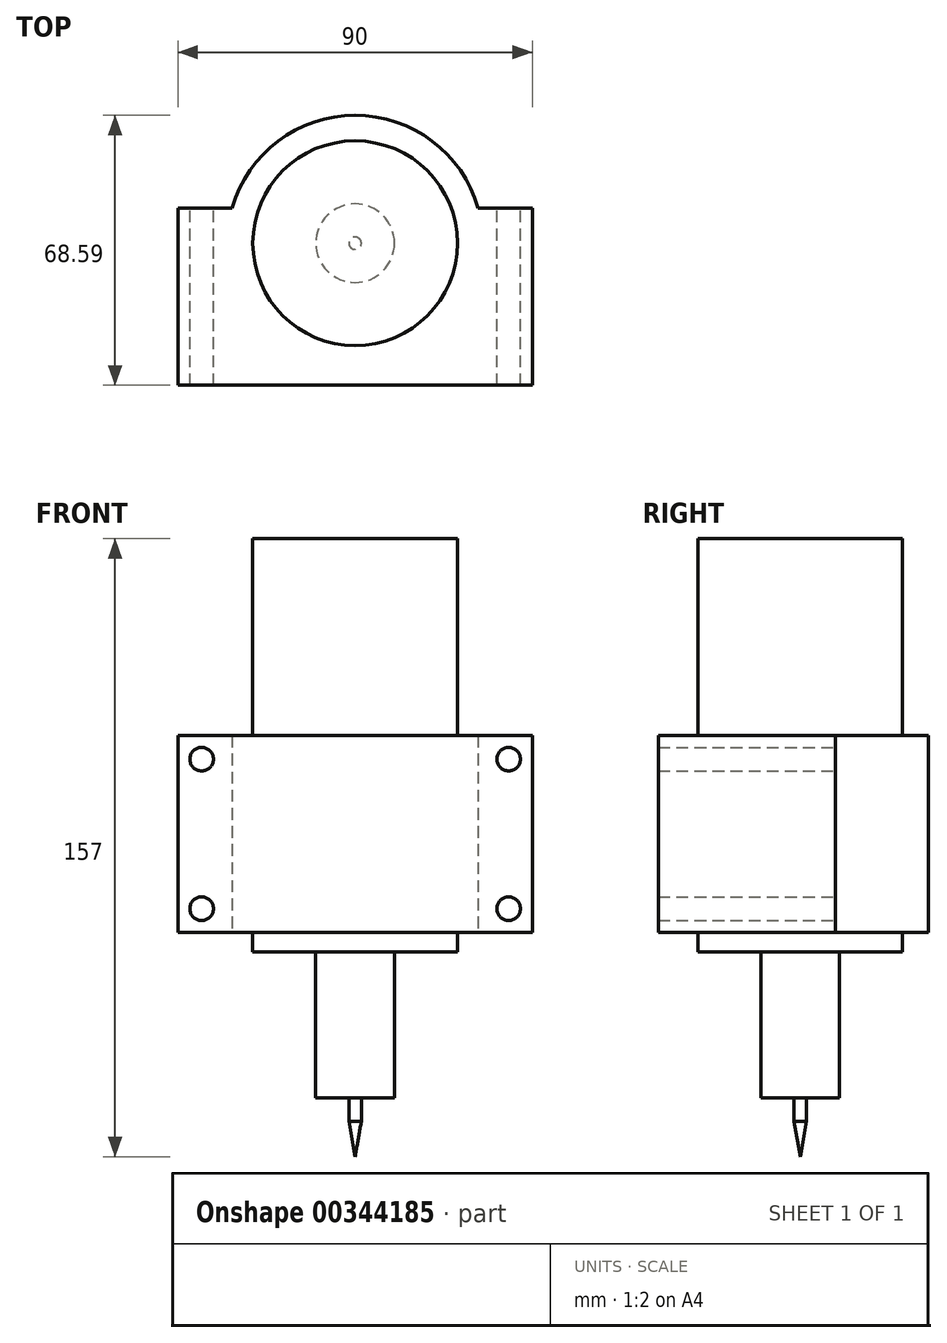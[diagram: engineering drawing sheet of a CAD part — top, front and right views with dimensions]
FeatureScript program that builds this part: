
annotation { "Feature Type Name" : "Feature", "Feature Type Description" : "" }
export const myFeature = defineFeature(function(context is Context, id is Id, definition is map)
    precondition{}
    {
        {
            var Q0;
            Q0=qCreatedBy(makeId("Top.planeOp"),FACE);
            var sketch = newSketch(context, id + "F0", { "sketchPlane" : qUnion([Q0])});
            skCircle(sketch, "E0", {"center": v(0, 0) * mm, "radius": 26 * mm});
            skSolve(sketch);
        }
        {
            var Q0;
            Q0 = qSketchRegion(id + "F0", true);
            extrude(context, id + "F1", {"entities" : qUnion([Q0]), "depth" : 105 * mm});
        }
        {
            var Q0;
            Q0=makeQuery(id+"F1.opExtrude","CAP_FACE",FACE,{"disambiguationData":[OSD([sQuery(id+"F0.wireOp",EDGE,"E0")])],"isStart":true});
            var sketch = newSketch(context, id + "F2", { "sketchPlane" : qUnion([Q0])});
            skCircle(sketch, "E1", {"center": v(0, 0) * mm, "radius": 10 * mm});
            skSolve(sketch);
        }
        {
            var Q0;
            Q0 = qSketchRegion(id + "F2", true);
            extrude(context, id + "F3", {"entities" : qUnion([Q0]), "operationType" : NewBodyOperationType.ADD, "depth" : 37 * mm});
        }
        {
            var Q0;
            Q0=qCreatedBy(makeId("Right.planeOp"),FACE);
            var sketch = newSketch(context, id + "F4", { "sketchPlane" : qUnion([Q0])});
            skLineSegment(sketch, "E2", {"start": v(0, -37) * mm, "end": v(0, -52) * mm});
            skLineSegment(sketch, "E3", {"start": v(0, -52) * mm, "end": v(-1.58, -43.04) * mm});
            skLineSegment(sketch, "E4", {"start": v(-1.58, -43.04) * mm, "end": v(-1.58, -37) * mm});
            skLineSegment(sketch, "E5", {"start": v(-1.58, -37) * mm, "end": v(0, -37) * mm});
            skPoint(sketch, "E6.orphan", {"position": v(0, -15.1) * mm});
            skSolve(sketch);
        }
        {
            var Q0;
            Q0 = qSketchRegion(id + "F4", true);
            var Q1;
            Q1=sQuery(id+"F4.wireOp",EDGE,"E2");
            revolve(context, id + "F5", {"operationType" : NewBodyOperationType.ADD, "entities" : qUnion([Q0]), "axis" : qUnion([Q1]), "revolveType" : RevolveType.FULL});
        }
        {
            var Q0;
            Q0=makeQuery(id+"F1.opExtrude","CAP_FACE",FACE,{"disambiguationData":[OSD([sQuery(id+"F0.wireOp",EDGE,"E0")])],"isStart":true});
            var sketch = newSketch(context, id + "F6", { "sketchPlane" : qUnion([Q0])});
            skArc(sketch, "E7", {"start": v(-31.24, -8.95) * mm, "mid": v(0, -32.5) * mm, "end": v(31.24, -8.95) * mm});
            skLineSegment(sketch, "E8.bottom", {"start": v(45, 36.1) * mm, "end": v(-45, 36.1) * mm});
            skLineSegment(sketch, "E8.top", {"start": v(45, -8.95) * mm, "end": v(31.24, -8.95) * mm});
            skLineSegment(sketch, "E8.left", {"start": v(45, 36.1) * mm, "end": v(45, -8.95) * mm});
            skLineSegment(sketch, "E8.right", {"start": v(-45, 36.1) * mm, "end": v(-45, -8.95) * mm});
            skPoint(sketch, "E8.middle", {"position": v(0, 13.57) * mm});
            skLineSegment(sketch, "E9.trimOffspring", {"start": v(-31.24, -8.95) * mm, "end": v(-45, -8.95) * mm});
            skSolve(sketch);
        }
        {
            var Q0;
            Q0 = qSketchRegion(id + "F6", true);
            extrude(context, id + "F7", {"entities" : qUnion([Q0]), "operationType" : NewBodyOperationType.ADD, "oppositeDirection" : true, "depth" : 55 * mm, "hasSecondDirection" : true, "secondDirectionOppositeDirection" : true, "secondDirectionDepth" : 5 * mm});
        }
        {
            var Q0;
            Q0=makeQuery(id+"F7.opExtrude","SWEPT_FACE",FACE,{"disambiguationData":[OSD([sQuery(id+"F6.wireOp",EDGE,"E8.top")])]});
            var sketch = newSketch(context, id + "F8", { "sketchPlane" : qUnion([Q0])});
            skCircle(sketch, "E10", {"center": v(-39, 49) * mm, "radius": 3 * mm});
            skCircle(sketch, "E11", {"center": v(-39, 11) * mm, "radius": 3 * mm});
            skCircle(sketch, "E12", {"center": v(39, 49) * mm, "radius": 3 * mm});
            skCircle(sketch, "E13", {"center": v(39, 11) * mm, "radius": 3 * mm});
            skSolve(sketch);
        }
        {
            var Q0;
            Q0 = qSketchRegion(id + "F8", true);
            extrude(context, id + "F9", {"entities" : qUnion([Q0]), "operationType" : NewBodyOperationType.REMOVE, "endBound" : BoundingType.THROUGH_ALL, "oppositeDirection" : true, "depth" : 25 * mm});
        }
    });
